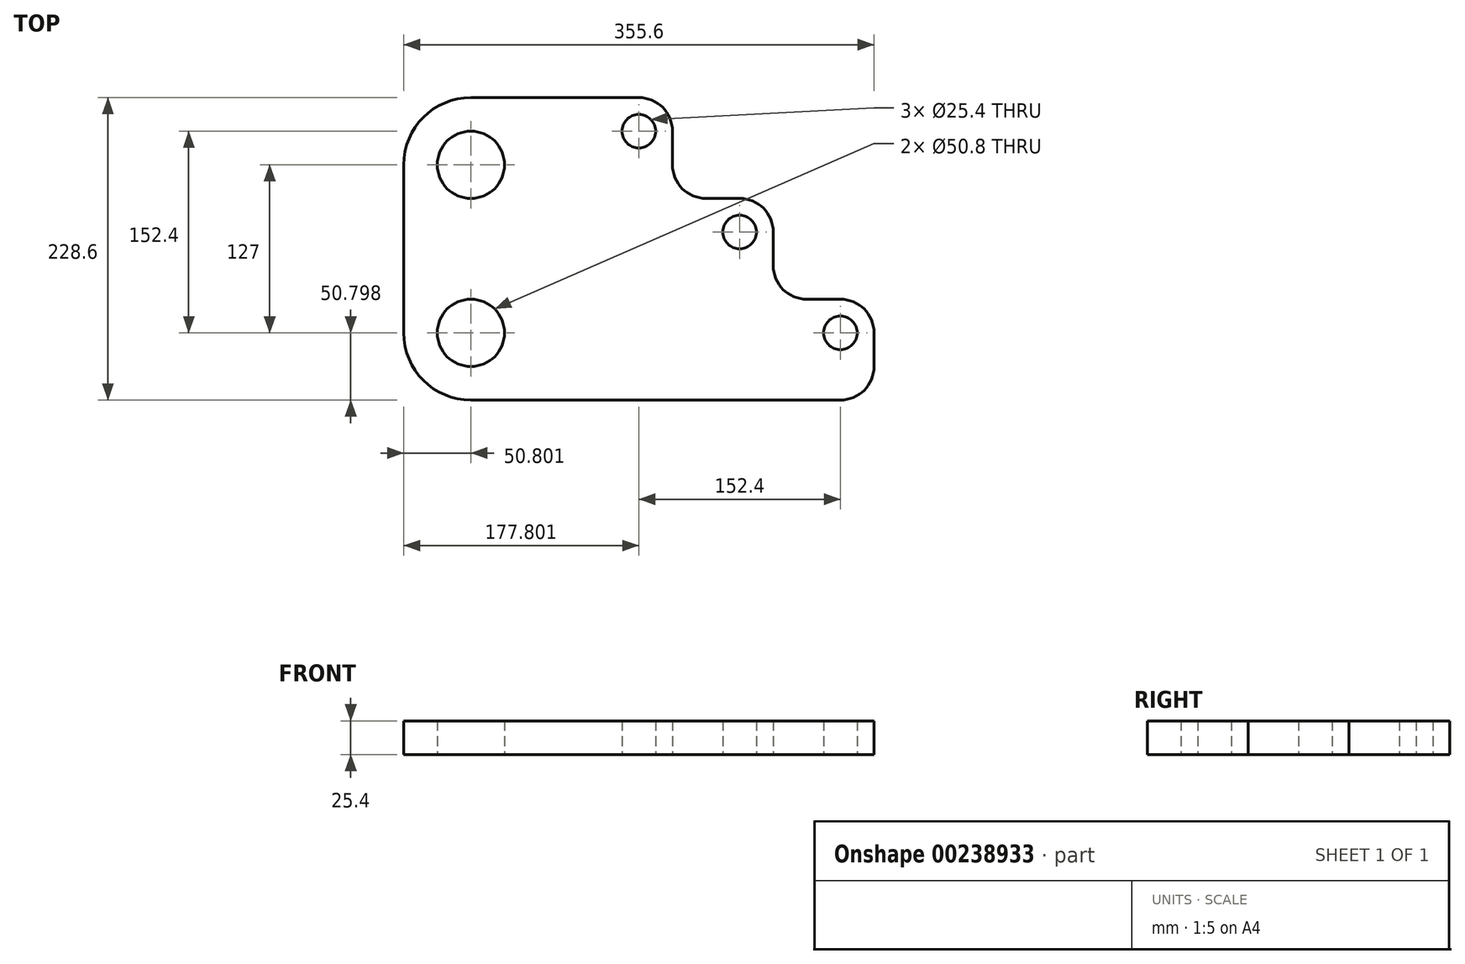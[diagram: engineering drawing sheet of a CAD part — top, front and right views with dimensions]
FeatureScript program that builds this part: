
annotation { "Feature Type Name" : "Feature", "Feature Type Description" : "" }
export const myFeature = defineFeature(function(context is Context, id is Id, definition is map)
    precondition{}
    {
        {
            var Q0;
            Q0=qCreatedBy(makeId("Top.planeOp"),FACE);
            var sketch = newSketch(context, id + "F0", { "sketchPlane" : qUnion([Q0])});
            skLineSegment(sketch, "E0", {"start": v(162.18, -55.96) * mm, "end": v(-117.22, -55.96) * mm});
            skLineSegment(sketch, "E1", {"start": v(-168.02, -5.16) * mm, "end": v(-168.02, 121.84) * mm});
            skLineSegment(sketch, "E2", {"start": v(-117.22, 172.64) * mm, "end": v(9.78, 172.64) * mm});
            skLineSegment(sketch, "E3", {"start": v(35.18, 147.24) * mm, "end": v(35.18, 121.84) * mm});
            skLineSegment(sketch, "E4", {"start": v(60.58, 96.44) * mm, "end": v(85.98, 96.44) * mm});
            skLineSegment(sketch, "E5", {"start": v(111.38, 71.04) * mm, "end": v(111.38, 45.64) * mm});
            skLineSegment(sketch, "E6", {"start": v(136.78, 20.24) * mm, "end": v(162.18, 20.24) * mm});
            skLineSegment(sketch, "E7", {"start": v(187.58, -5.16) * mm, "end": v(187.58, -30.56) * mm});
            skPoint(sketch, "E8.visualSharp", {"position": v(-168.02, 172.64) * mm});
            skArc(sketch, "E8.filletArc", {"start": v(-117.22, 172.64) * mm, "mid": v(-153.14, 157.76) * mm, "end": v(-168.02, 121.84) * mm});
            skPoint(sketch, "E9.visualSharp", {"position": v(-168.02, -55.96) * mm});
            skArc(sketch, "E9.filletArc", {"start": v(-168.02, -5.16) * mm, "mid": v(-153.14, -41.08) * mm, "end": v(-117.22, -55.96) * mm});
            skPoint(sketch, "E10.visualSharp", {"position": v(187.58, -55.96) * mm});
            skArc(sketch, "E10.filletArc", {"start": v(162.18, -55.96) * mm, "mid": v(180.14, -48.52) * mm, "end": v(187.58, -30.56) * mm});
            skPoint(sketch, "E11.visualSharp", {"position": v(187.58, 20.24) * mm});
            skArc(sketch, "E11.filletArc", {"start": v(187.58, -5.16) * mm, "mid": v(180.14, 12.8) * mm, "end": v(162.18, 20.24) * mm});
            skPoint(sketch, "E12.visualSharp", {"position": v(111.38, 20.24) * mm});
            skArc(sketch, "E12.filletArc", {"start": v(111.38, 45.64) * mm, "mid": v(118.82, 27.68) * mm, "end": v(136.78, 20.24) * mm});
            skPoint(sketch, "E13.visualSharp", {"position": v(111.38, 96.44) * mm});
            skArc(sketch, "E13.filletArc", {"start": v(111.38, 71.04) * mm, "mid": v(103.94, 89) * mm, "end": v(85.98, 96.44) * mm});
            skPoint(sketch, "E14.visualSharp", {"position": v(35.18, 96.44) * mm});
            skArc(sketch, "E14.filletArc", {"start": v(35.18, 121.84) * mm, "mid": v(42.62, 103.88) * mm, "end": v(60.58, 96.44) * mm});
            skPoint(sketch, "E15.visualSharp", {"position": v(35.18, 172.64) * mm});
            skArc(sketch, "E15.filletArc", {"start": v(35.18, 147.24) * mm, "mid": v(27.74, 165.2) * mm, "end": v(9.78, 172.64) * mm});
            skCircle(sketch, "E16", {"center": v(-117.22, 121.84) * mm, "radius": 25.4 * mm});
            skCircle(sketch, "E17", {"center": v(-117.22, -5.16) * mm, "radius": 25.4 * mm});
            skCircle(sketch, "E18", {"center": v(9.78, 147.24) * mm, "radius": 12.7 * mm});
            skCircle(sketch, "E19", {"center": v(85.98, 71.04) * mm, "radius": 12.7 * mm});
            skCircle(sketch, "E20", {"center": v(162.18, -5.16) * mm, "radius": 12.7 * mm});
            skSolve(sketch);
        }
        {
            var Q0;
            Q0 = qSketchRegion(id + "F0", true);
            extrude(context, id + "F1", {"entities" : qUnion([Q0]), "depth" : 25.4 * mm});
        }
    });
